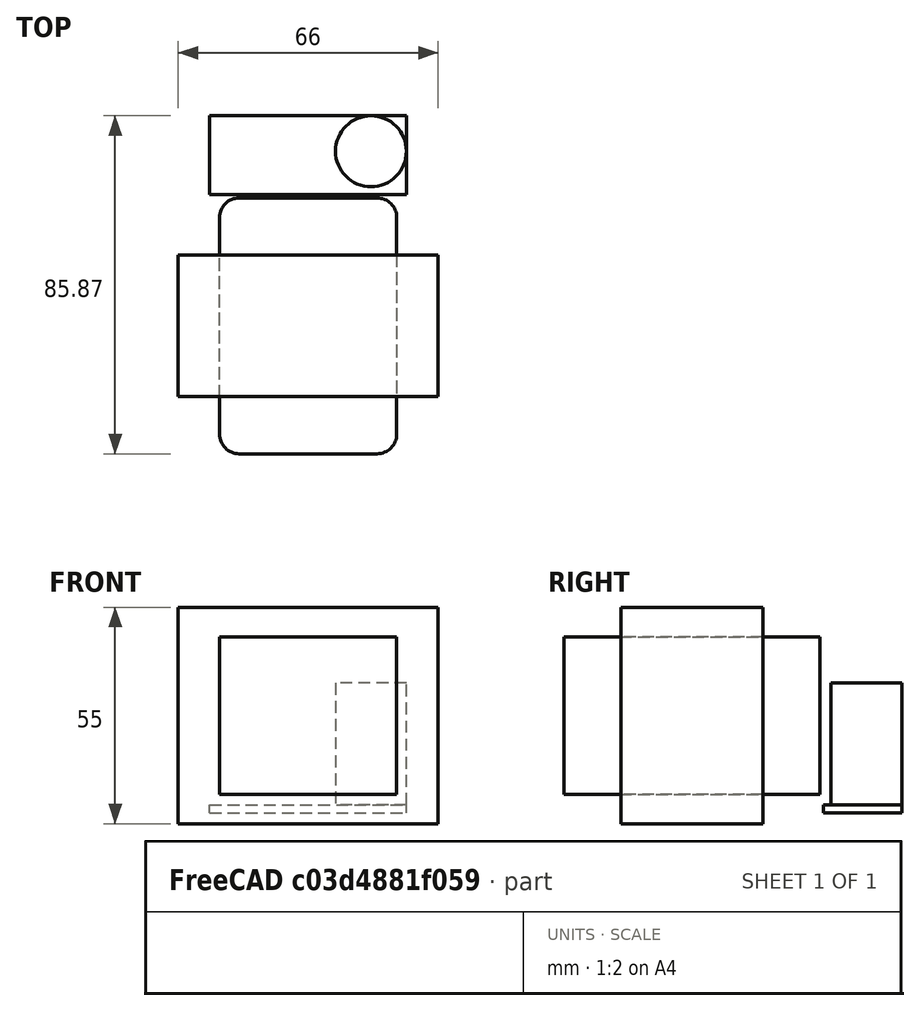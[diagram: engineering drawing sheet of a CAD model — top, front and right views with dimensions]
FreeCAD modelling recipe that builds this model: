
FCSTD DOCUMENT  (FreeCAD 0.18.4R)
Label: PSU Assembly
License: All rights reserved
LicenseURL: http://en.wikipedia.org/wiki/All_rights_reserved
objects: Part::FeaturePython×2, Part::MultiFuse×1
note: 3 computed .brp shape members not serialized (recipe doc carries the construction recipe); baked Part::Feature solids carry a one-line shape summary decoded from their .brp

FEATURE [Part::FeaturePython] b_Trafo_001_  label="Trafo_001"  # a2plus imported part (geometry in sourceFile) (typed FeaturePython)
  a2p_Version = V0.1
  fixedPosition = true
  objectType = a2pPart
  sourceFile = ./Trafo.FCStd
  subassemblyImport = false
  timeLastImport = 1.59605e+09
  updateColors = true
FEATURE [Part::FeaturePython] b_Rectifier_001_  label="Rectifier_001"  # a2plus imported part (geometry in sourceFile) (typed FeaturePython)
  Placement = pos=(-0.0330048,43.3683,-24.7265) rot=(-1,0,1e-06;0rad)
  a2p_Version = V0.1
  fixedPosition = false
  objectType = a2pPart
  sourceFile = ./Rectifier.FCStd
  subassemblyImport = false
  timeLastImport = 1.59605e+09
  updateColors = true
FEATURE [Part::MultiFuse] Fusion
  Shapes = -> [b_Trafo_001_,b_Rectifier_001_]
